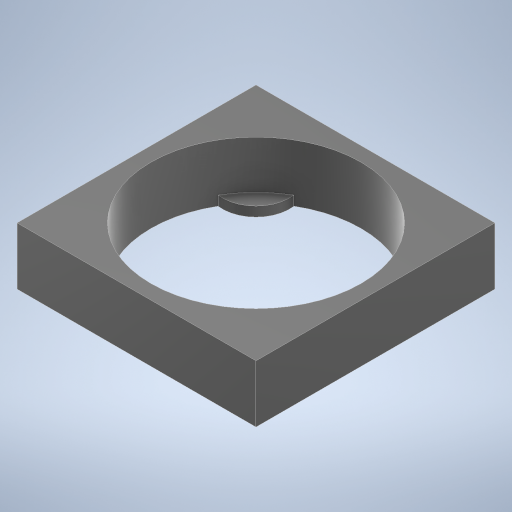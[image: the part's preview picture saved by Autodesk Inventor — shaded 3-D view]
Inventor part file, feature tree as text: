
AUTODESK INVENTOR PART (.ipt)
format: ipt  version: 2024.2 (Build 282272000, 272)  size: 314,880 bytes
history: native  units: in
note: dims shown in document units (in); Inventor stores cm internally (conversion verified against a paired STEP export)
features: extrude x2, sketch x1, pattern_linear x1
ambient origin geometry x8: Origin, YZ Plane, XZ Plane, XY Plane, X Axis, Y Axis, Z Axis, Center Point
bodies: Body1 (feature_tree)
feature tree (4):
  sketch  "Sketch1"  dims[d18=0.0in d20=0.0in d27=0.2756in d28=0.2756in d29=0.2756in d30=3.937in d32=0.9843in d33=1.5748in d35=0.9843in d36=0.9843in d37=0.9843in d17=0.5in d19=0.5in d21=0.5in d22=0.0344in d31=0.0344in d38=0.5in d39=0.0344in d40=0.5in d41=0.0344in]
  extrude  "thickness"  TaperAngle=0.0deg  [1 undecoded]
  extrude  "catcher"  Depth=0.9843in
  pattern_linear  "gridPattern"  Spacing1=0.2756in  [1 undecoded]
note: 2 required parameter values undecoded (feature->parameter linkage not recoverable at this tier; creation-order binding heuristic only, values carry confidence <= 0.55)
